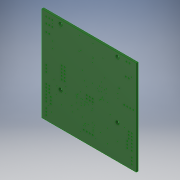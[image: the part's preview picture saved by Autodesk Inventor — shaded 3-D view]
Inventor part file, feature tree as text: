
AUTODESK INVENTOR PART (.ipt)
format: ipt  version: 2019 (Build 230136000, 136)  size: 343,040 bytes
history: native  units: mm
features: extrude x1, sketch x1
ambient origin geometry x8: Origin, YZ Plane, XZ Plane, XY Plane, X Axis, Y Axis, Z Axis, Center Point
bodies: Solid1 (feature_tree)
feature tree (2):
  extrude  "Kama Sterownik v1.brd_Outline"  [1 undecoded]
  sketch  "Sketch1"  dims[d0=1.6mm d1=0.0mm]
note: 1 required parameter value undecoded (feature->parameter linkage not recoverable at this tier; creation-order binding heuristic only, values carry confidence <= 0.55)
